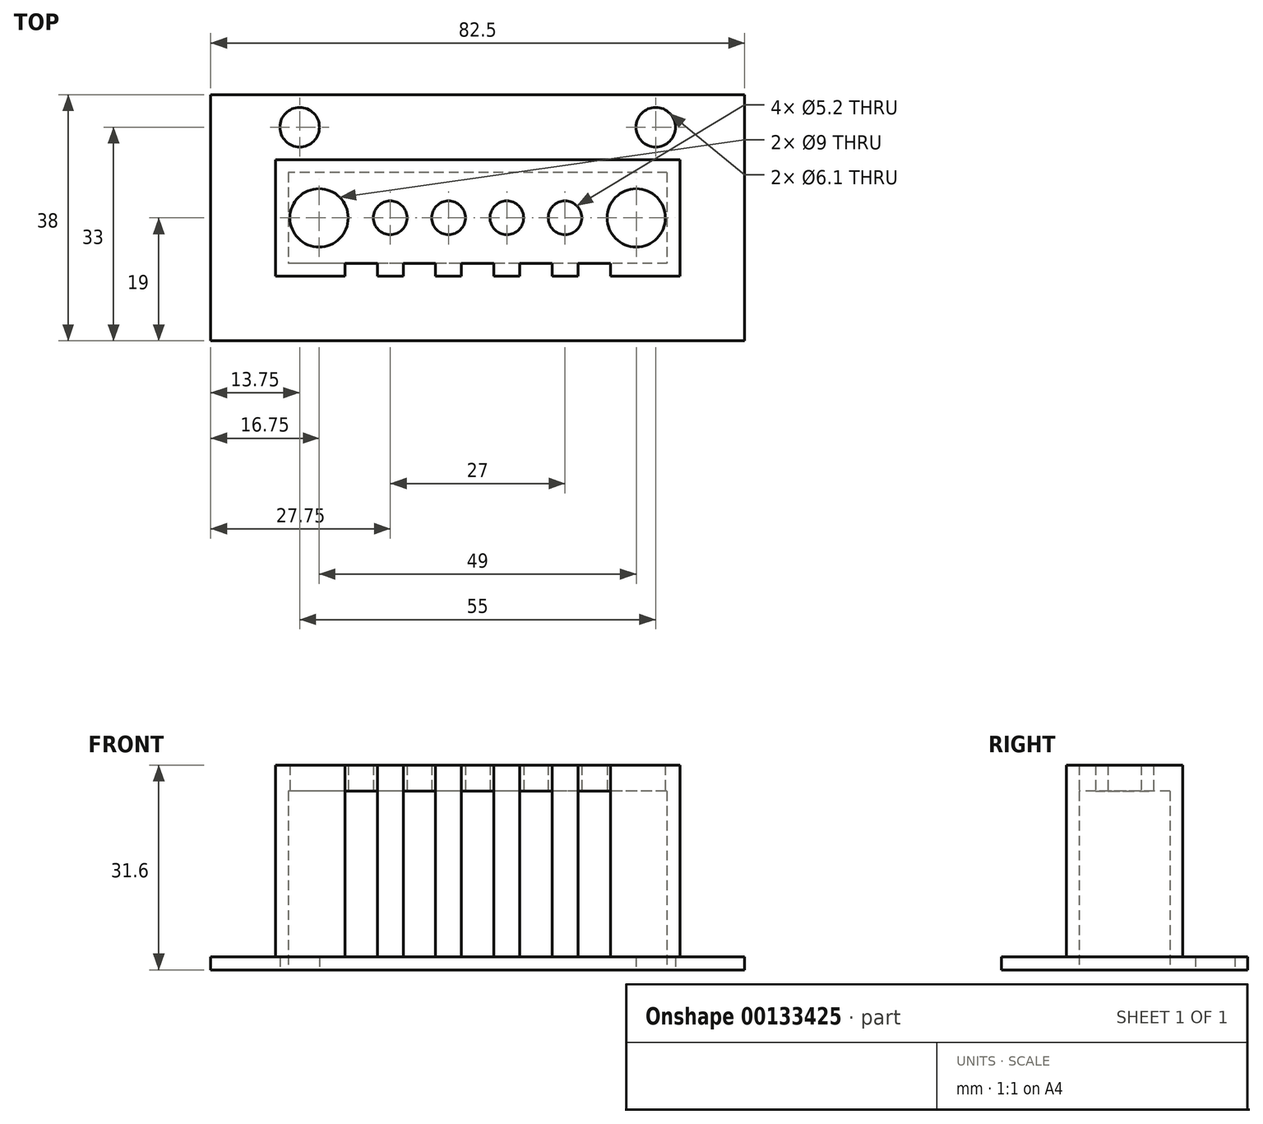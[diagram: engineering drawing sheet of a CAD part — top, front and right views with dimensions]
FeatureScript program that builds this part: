
annotation { "Feature Type Name" : "Feature", "Feature Type Description" : "" }
export const myFeature = defineFeature(function(context is Context, id is Id, definition is map)
    precondition{}
    {
        {
            var Q0;
            Q0=qCreatedBy(makeId("Top.planeOp"),FACE);
            var sketch = newSketch(context, id + "F0", { "sketchPlane" : qUnion([Q0])});
            skLineSegment(sketch, "E0.bottom", {"start": v(31.25, 9) * mm, "end": v(-31.25, 9) * mm});
            skLineSegment(sketch, "E0.top", {"start": v(31.25, -9) * mm, "end": v(-31.25, -9) * mm});
            skLineSegment(sketch, "E0.left", {"start": v(31.25, 9) * mm, "end": v(31.25, -9) * mm});
            skLineSegment(sketch, "E0.right", {"start": v(-31.25, 9) * mm, "end": v(-31.25, -9) * mm});
            skPoint(sketch, "E0.middle", {"position": v(0, 0) * mm});
            skLineSegment(sketch, "E1", {"start": v(-31.25, -9) * mm, "end": v(-31.25, 0) * mm});
            skLineSegment(sketch, "E2", {"start": v(-31.25, 0) * mm, "end": v(31.25, 0) * mm});
            skLineSegment(sketch, "E3", {"start": v(-13.5, 0) * mm, "end": v(-4.5, 0) * mm, "construction": true});
            skCircle(sketch, "E4", {"center": v(-4.5, 0) * mm, "radius": 2.6 * mm});
            skCircle(sketch, "E5.MirrorC", {"center": v(4.5, 0) * mm, "radius": 2.6 * mm});
            skLineSegment(sketch, "E6.0", {"start": v(29.25, -7) * mm, "end": v(-29.25, -7) * mm});
            skLineSegment(sketch, "E6.1", {"start": v(29.25, 7) * mm, "end": v(29.25, -7) * mm});
            skLineSegment(sketch, "E6.2", {"start": v(29.25, 7) * mm, "end": v(-29.25, 7) * mm});
            skLineSegment(sketch, "E6.3", {"start": v(-29.25, 7) * mm, "end": v(-29.25, -7) * mm});
            skCircle(sketch, "E7", {"center": v(-13.5, 0) * mm, "radius": 2.6 * mm});
            skLineSegment(sketch, "E8", {"start": v(4.5, 0) * mm, "end": v(4.5, 0) * mm});
            skCircle(sketch, "E9.MirrorC", {"center": v(13.5, 0) * mm, "radius": 2.6 * mm});
            skLineSegment(sketch, "E10.0", {"start": v(41.25, 19) * mm, "end": v(-41.25, 19) * mm});
            skLineSegment(sketch, "E10.1", {"start": v(41.25, 19) * mm, "end": v(41.25, -19) * mm});
            skLineSegment(sketch, "E10.2", {"start": v(41.25, -19) * mm, "end": v(-41.25, -19) * mm});
            skLineSegment(sketch, "E10.3", {"start": v(-41.25, 19) * mm, "end": v(-41.25, -19) * mm});
            skLineSegment(sketch, "E11", {"start": v(-41.25, 19) * mm, "end": v(-41.25, 14) * mm});
            skLineSegment(sketch, "E12", {"start": v(-41.25, 14) * mm, "end": v(-36.25, 14) * mm});
            skLineSegment(sketch, "E13", {"start": v(-13.5, 0) * mm, "end": v(-36.25, 0) * mm});
            skLineSegment(sketch, "E14", {"start": v(-36.25, 0) * mm, "end": v(-36.25, 14) * mm});
            skCircle(sketch, "E15.MirrorC", {"center": v(27.5, 14) * mm, "radius": 3.05 * mm});
            skCircle(sketch, "E16.MirrorC", {"center": v(-27.5, 14) * mm, "radius": 3.05 * mm});
            skLineSegment(sketch, "E17", {"start": v(0, 0) * mm, "end": v(24.5, 0) * mm});
            skCircle(sketch, "E18", {"center": v(24.5, 0) * mm, "radius": 4.5 * mm});
            skCircle(sketch, "E19.MirrorC", {"center": v(-24.5, 0) * mm, "radius": 4.5 * mm});
            skSolve(sketch);
        }
        {
            var Q0;
            {var subQ8=sQuery(id+"F0.wireOp",EDGE,"E0.top");Q0=makeQuery(id+"F0.imprint","IMPRINT",FACE,{"disambiguationData":[TD([[makeQuery(id+"F0.imprint","IMPRINT",EDGE,{"derivedFrom":subQ8}),-1.0]])]});}
            var Q1;
            {var subQ6=sQuery(id+"F0.wireOp",EDGE,"E0.bottom");Q1=makeQuery(id+"F0.imprint","IMPRINT",FACE,{"disambiguationData":[TD([[makeQuery(id+"F0.imprint","IMPRINT",EDGE,{"derivedFrom":subQ6}),1.0]])]});}
            extrude(context, id + "F1", {"entities" : qUnion([Q0, Q1]), "depth" : 31.6 * mm});
        }
        {
            var Q0;
            {var subQ8=sQuery(id+"F0.wireOp",EDGE,"E6.2");Q0=makeQuery(id+"F0.imprint","IMPRINT",FACE,{"disambiguationData":[TD([[makeQuery(id+"F0.imprint","IMPRINT",EDGE,{"derivedFrom":subQ8}),1.0]])]});}
            var Q1;
            {var subQ0=sQuery(id+"F0.wireOp",EDGE,"E6.0");Q1=makeQuery(id+"F0.imprint","IMPRINT",FACE,{"disambiguationData":[TD([[makeQuery(id+"F0.imprint","IMPRINT",EDGE,{"derivedFrom":subQ0}),-1.0]])]});}
            extrude(context, id + "F2", {"entities" : qUnion([Q0, Q1]), "operationType" : NewBodyOperationType.ADD, "depth" : 31.6 * mm, "hasSecondDirection" : true, "secondDirectionOppositeDirection" : false, "secondDirectionDepth" : 27.6 * mm});
        }
        {
            var Q0;
            {var subQ0=sQuery(id+"F0.wireOp",EDGE,"E0.bottom");Q0=makeQuery(id+"F0.imprint","IMPRINT",FACE,{"disambiguationData":[TD([[makeQuery(id+"F0.imprint","IMPRINT",EDGE,{"derivedFrom":subQ0}),-1.0]])]});}
            extrude(context, id + "F3", {"entities" : qUnion([Q0]), "operationType" : NewBodyOperationType.ADD, "depth" : 2 * mm});
        }
        {
            var Q0;
            Q0=makeQuery(id+"F1.opExtrude","SWEPT_FACE",FACE,{"disambiguationData":[OSD([sQuery(id+"F0.wireOp",EDGE,"E0.top")])]});
            var sketch = newSketch(context, id + "F4", { "sketchPlane" : qUnion([Q0])});
            skLineSegment(sketch, "E20", {"start": v(0, 2) * mm, "end": v(0, 31.6) * mm});
            skLineSegment(sketch, "E21.bottom", {"start": v(2.5, 31.6) * mm, "end": v(-2.5, 31.6) * mm});
            skLineSegment(sketch, "E21.top", {"start": v(2.5, 2) * mm, "end": v(-2.5, 2) * mm});
            skLineSegment(sketch, "E21.left", {"start": v(2.5, 31.6) * mm, "end": v(2.5, 2) * mm});
            skLineSegment(sketch, "E21.right", {"start": v(-2.5, 31.6) * mm, "end": v(-2.5, 2) * mm});
            skPoint(sketch, "E21.middle", {"position": v(0, 16.8) * mm});
            skLineSegment(sketch, "E22", {"start": v(0, 2) * mm, "end": v(-9, 2) * mm});
            skLineSegment(sketch, "E23", {"start": v(0, 2) * mm, "end": v(9, 2) * mm});
            skLineSegment(sketch, "E24", {"start": v(9, 2) * mm, "end": v(18, 2) * mm});
            skLineSegment(sketch, "E25", {"start": v(-9, 2) * mm, "end": v(-18, 2) * mm});
            skLineSegment(sketch, "E26", {"start": v(-18, 2) * mm, "end": v(-18, 31.6) * mm});
            skLineSegment(sketch, "E27", {"start": v(-9, 2) * mm, "end": v(-9, 31.6) * mm});
            skLineSegment(sketch, "E28", {"start": v(9, 2) * mm, "end": v(9, 31.6) * mm});
            skLineSegment(sketch, "E29", {"start": v(18, 2) * mm, "end": v(18, 31.6) * mm});
            skLineSegment(sketch, "E30.bottom", {"start": v(-15.5, 31.6) * mm, "end": v(-20.5, 31.6) * mm});
            skLineSegment(sketch, "E30.top", {"start": v(-15.5, 2) * mm, "end": v(-20.5, 2) * mm});
            skLineSegment(sketch, "E30.left", {"start": v(-15.5, 31.6) * mm, "end": v(-15.5, 2) * mm});
            skLineSegment(sketch, "E30.right", {"start": v(-20.5, 31.6) * mm, "end": v(-20.5, 2) * mm});
            skPoint(sketch, "E30.middle", {"position": v(-18, 16.8) * mm});
            skLineSegment(sketch, "E31.bottom", {"start": v(-6.5, 31.6) * mm, "end": v(-11.5, 31.6) * mm});
            skLineSegment(sketch, "E31.top", {"start": v(-6.5, 2) * mm, "end": v(-11.5, 2) * mm});
            skLineSegment(sketch, "E31.left", {"start": v(-6.5, 31.6) * mm, "end": v(-6.5, 2) * mm});
            skLineSegment(sketch, "E31.right", {"start": v(-11.5, 31.6) * mm, "end": v(-11.5, 2) * mm});
            skPoint(sketch, "E31.middle", {"position": v(-9, 16.8) * mm});
            skLineSegment(sketch, "E32.bottom", {"start": v(11.5, 31.6) * mm, "end": v(6.5, 31.6) * mm});
            skLineSegment(sketch, "E32.top", {"start": v(11.5, 2) * mm, "end": v(6.5, 2) * mm});
            skLineSegment(sketch, "E32.left", {"start": v(11.5, 31.6) * mm, "end": v(11.5, 2) * mm});
            skLineSegment(sketch, "E32.right", {"start": v(6.5, 31.6) * mm, "end": v(6.5, 2) * mm});
            skPoint(sketch, "E32.middle", {"position": v(9, 16.8) * mm});
            skLineSegment(sketch, "E33.bottom", {"start": v(20.5, 31.6) * mm, "end": v(15.5, 31.6) * mm});
            skLineSegment(sketch, "E33.top", {"start": v(20.5, 2) * mm, "end": v(15.5, 2) * mm});
            skLineSegment(sketch, "E33.left", {"start": v(20.5, 31.6) * mm, "end": v(20.5, 2) * mm});
            skLineSegment(sketch, "E33.right", {"start": v(15.5, 31.6) * mm, "end": v(15.5, 2) * mm});
            skPoint(sketch, "E33.middle", {"position": v(18, 16.8) * mm});
            skSolve(sketch);
        }
        {
            var Q0;
            {var subQ0=sQuery(id+"F4.wireOp",EDGE,"E20");Q0=makeQuery(id+"F4.imprint","IMPRINT",FACE,{"disambiguationData":[TD([[makeQuery(id+"F4.imprint","IMPRINT",EDGE,{"derivedFrom":subQ0}),1.0]])]});}
            var Q1;
            {var subQ0=sQuery(id+"F4.wireOp",EDGE,"E20");Q1=makeQuery(id+"F4.imprint","IMPRINT",FACE,{"disambiguationData":[TD([[makeQuery(id+"F4.imprint","IMPRINT",EDGE,{"derivedFrom":subQ0}),-1.0]])]});}
            var Q2;
            {var subQ0=sQuery(id+"F4.wireOp",EDGE,"E26");Q2=makeQuery(id+"F4.imprint","IMPRINT",FACE,{"disambiguationData":[TD([[makeQuery(id+"F4.imprint","IMPRINT",EDGE,{"derivedFrom":subQ0}),1.0]])]});}
            var Q3;
            {var subQ0=sQuery(id+"F4.wireOp",EDGE,"E26");Q3=makeQuery(id+"F4.imprint","IMPRINT",FACE,{"disambiguationData":[TD([[makeQuery(id+"F4.imprint","IMPRINT",EDGE,{"derivedFrom":subQ0}),-1.0]])]});}
            var Q4;
            {var subQ0=sQuery(id+"F4.wireOp",EDGE,"E27");Q4=makeQuery(id+"F4.imprint","IMPRINT",FACE,{"disambiguationData":[TD([[makeQuery(id+"F4.imprint","IMPRINT",EDGE,{"derivedFrom":subQ0}),1.0]])]});}
            var Q5;
            {var subQ0=sQuery(id+"F4.wireOp",EDGE,"E27");Q5=makeQuery(id+"F4.imprint","IMPRINT",FACE,{"disambiguationData":[TD([[makeQuery(id+"F4.imprint","IMPRINT",EDGE,{"derivedFrom":subQ0}),-1.0]])]});}
            var Q6;
            {var subQ0=sQuery(id+"F4.wireOp",EDGE,"E28");Q6=makeQuery(id+"F4.imprint","IMPRINT",FACE,{"disambiguationData":[TD([[makeQuery(id+"F4.imprint","IMPRINT",EDGE,{"derivedFrom":subQ0}),-1.0]])]});}
            var Q7;
            {var subQ0=sQuery(id+"F4.wireOp",EDGE,"E28");Q7=makeQuery(id+"F4.imprint","IMPRINT",FACE,{"disambiguationData":[TD([[makeQuery(id+"F4.imprint","IMPRINT",EDGE,{"derivedFrom":subQ0}),1.0]])]});}
            var Q8;
            {var subQ0=sQuery(id+"F4.wireOp",EDGE,"E29");Q8=makeQuery(id+"F4.imprint","IMPRINT",FACE,{"disambiguationData":[TD([[makeQuery(id+"F4.imprint","IMPRINT",EDGE,{"derivedFrom":subQ0}),1.0]])]});}
            var Q9;
            {var subQ0=sQuery(id+"F4.wireOp",EDGE,"E29");Q9=makeQuery(id+"F4.imprint","IMPRINT",FACE,{"disambiguationData":[TD([[makeQuery(id+"F4.imprint","IMPRINT",EDGE,{"derivedFrom":subQ0}),-1.0]])]});}
            extrude(context, id + "F5", {"entities" : qUnion([Q0, Q1, Q2, Q3, Q4, Q5, Q6, Q7, Q8, Q9]), "operationType" : NewBodyOperationType.REMOVE, "oppositeDirection" : true, "depth" : 2 * mm});
        }
    });
